# Revit family: SANINDUSA_134700004_Look_45LookCornerWallMountedBasin45x48_V0
name_source: partatom
category: Plumbing Fixtures
units: mm (PartAtom-declared; Revit-internal decimal feet)

## family parameters
Cut with Voids When Loaded = No
Host = Face
Part Type = Normal
Room Calculation Point = No
Round Connector Dimension = Use Diameter
Shared = No

## types (1)
- SANINDUSA_134700004_Look_45LookCornerWallMountedBasin45x48_V0
    AssetType = Fixed
    Category = Pr_40_20_96_18: Counter top wash basins
    CodePerformance = EN 14688:2006  CL 25
    Color = white
    Constituents = With embellisher ring and fixing kit (included).
    Default Elevation = 1219 mm
    Description = Waste water appliance for washing the upper parts of the body.
    DrainSize = 46 mm  [stored 0.150919 ft]
    Element Type = WASHHANDBASIN: Waste water appliance for washing the upper parts of the body.
    Features = "Installation wall-mounted. Glazed on all sides except on the backside, drain, and on the lower setting place of the mixer. With embellished ring. Not rectified."
    Finish = gloss
    Installation Instructions = https://www.tec.sanindusa.pt
    Manufacturer = Sanindusa
    ManufacturerName = Sanindusa
    ManufacturerURL = www.tec.sanindusa.pt
    Material = vitreous china
    Model = 134700004
    ModelNumber = 134700004
    ModelReference = Look
    Name = 45 Look corner washbasin
    NominalDepth = 112 mm  [stored 0.367454 ft]
    NominalHeight = 162 mm  [stored 0.531496 ft]
    NominalLength = 445 mm  [stored 1.45997 ft]
    NominalWidth = 480 mm  [stored 1.5748 ft]
    Pre-defined type (IFC) = WASHHANDBASIN
    ProductInformation = https://www.tec.sanindusa.pt
    ProductionYear = 2014
    Size = 45x48
    SpilloverLevel = 68
    Type (IFC) = IfcSanitaryTerminalType
    URL = www.tec.sanindusa.pt
    Version = 1
    WarrantyDescription = https://www.tec.sanindusa.pt
    WarrantyDurationParts = 5
    WarrantyDurationUnit = year
    WashHandBasinMounting = wallhung
    WashHandBasinType = handrinse
    Waste Connection = Yes
    Weight = 10.30 kg

note: [stored X ft] marks values corroborated as IEEE doubles in the binary element streams (Revit-internal decimal feet)

## geometry (parser evidence)
native form markers: Sweep x8
no freeform markers — native parametric forms only
